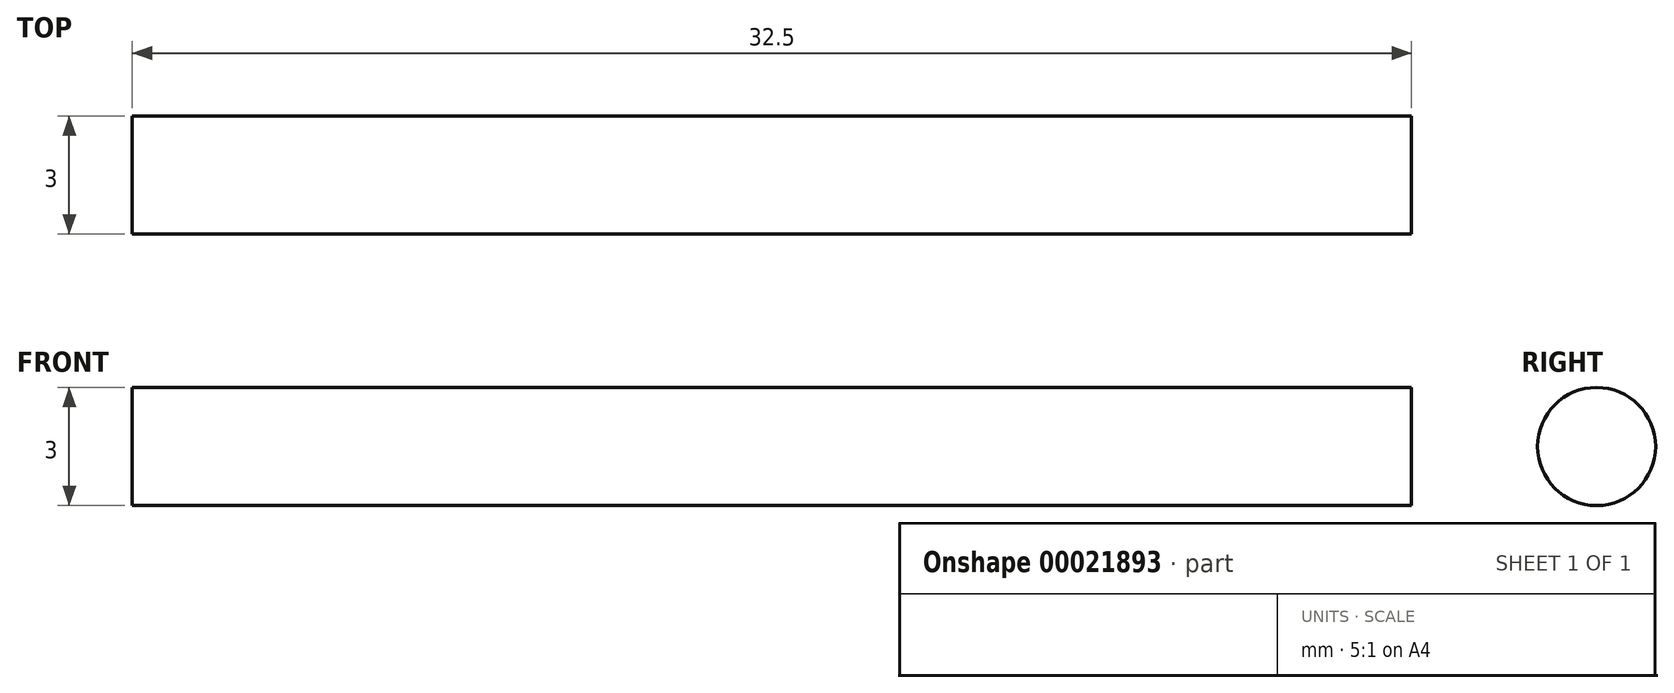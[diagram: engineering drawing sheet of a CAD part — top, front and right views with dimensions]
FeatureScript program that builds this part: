
annotation { "Feature Type Name" : "Feature", "Feature Type Description" : "" }
export const myFeature = defineFeature(function(context is Context, id is Id, definition is map)
    precondition{}
    {
        {
            var Q0;
            Q0=qCreatedBy(makeId("Front.planeOp"),FACE);
            var sketch = newSketch(context, id + "F0", { "sketchPlane" : qUnion([Q0])});
            skLineSegment(sketch, "E0", {"start": v(-16.25, 0) * mm, "end": v(16.25, 0) * mm});
            skLineSegment(sketch, "E1", {"start": v(0, 0) * mm, "end": v(0, -1.5) * mm});
            skLineSegment(sketch, "E2", {"start": v(0, -1.5) * mm, "end": v(16.25, -1.5) * mm});
            skLineSegment(sketch, "E3", {"start": v(0, -1.5) * mm, "end": v(-16.25, -1.5) * mm});
            skLineSegment(sketch, "E4", {"start": v(-16.25, 0) * mm, "end": v(-16.25, -1.5) * mm});
            skLineSegment(sketch, "E5", {"start": v(16.25, 0) * mm, "end": v(16.25, -1.5) * mm});
            skSolve(sketch);
        }
        {
            var Q0;
            {var subQ1=sQuery(id+"F0.wireOp",EDGE,"E1");Q0=makeQuery(id+"F0.imprint","IMPRINT",FACE,{"disambiguationData":[TD([[makeQuery(id+"F0.imprint","IMPRINT",EDGE,{"derivedFrom":subQ1}),-1.0]])]});}
            var Q1;
            {var subQ1=sQuery(id+"F0.wireOp",EDGE,"E1");Q1=makeQuery(id+"F0.imprint","IMPRINT",FACE,{"disambiguationData":[TD([[makeQuery(id+"F0.imprint","IMPRINT",EDGE,{"derivedFrom":subQ1}),1.0]])]});}
            var Q2;
            Q2=sQuery(id+"F0.wireOp",EDGE,"E2");
            revolve(context, id + "F1", {"entities" : qUnion([Q0, Q1]), "axis" : qUnion([Q2]), "revolveType" : RevolveType.FULL});
        }
    });
